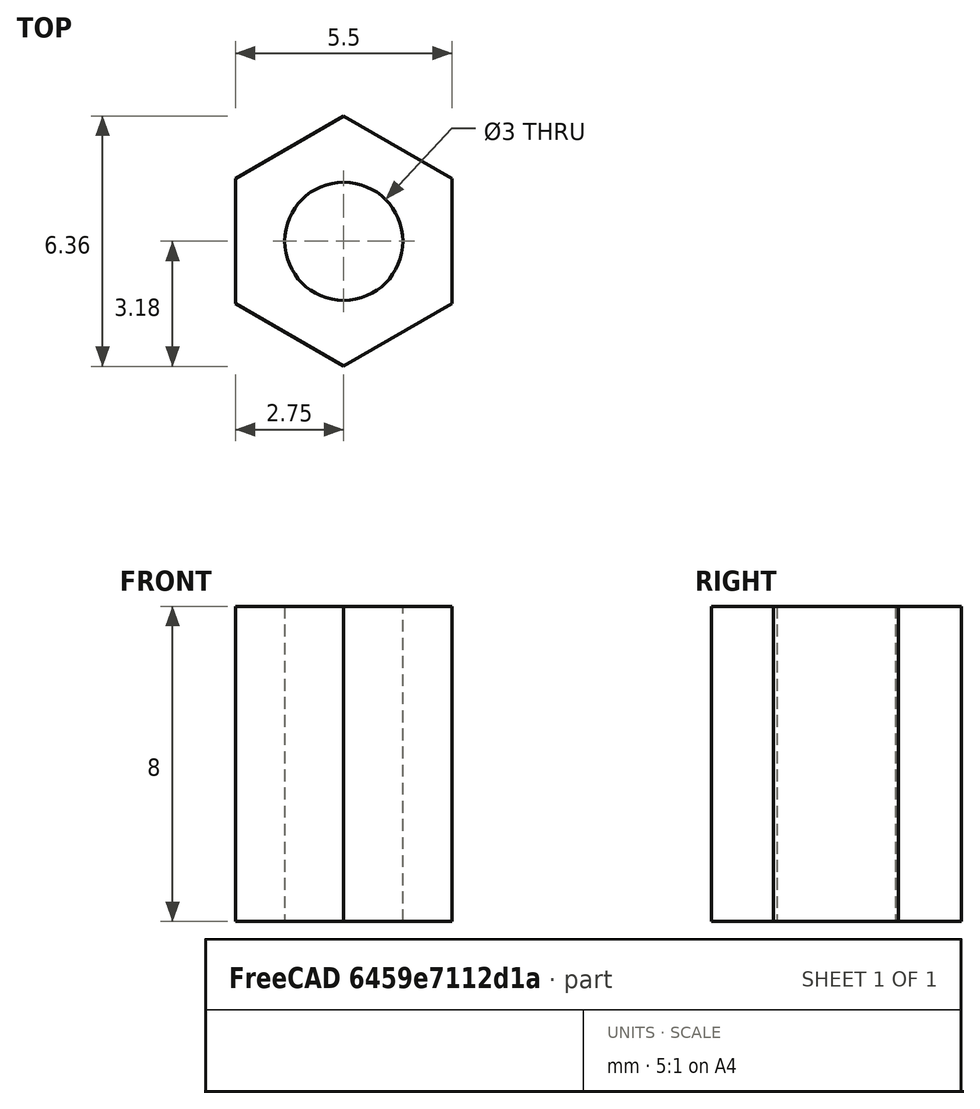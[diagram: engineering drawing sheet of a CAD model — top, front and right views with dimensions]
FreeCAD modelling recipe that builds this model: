
FCSTD DOCUMENT  (FreeCAD 0.20R29177 (Git))
Label: colonetteM3x8
License: All rights reserved
LicenseURL: http://en.wikipedia.org/wiki/All_rights_reserved
objects: Spreadsheet::Sheet×1, Sketcher::SketchObject×1, PartDesign::Pad×1, PartDesign::Body×1, App::Part×1
note: 4 computed .brp shape members not serialized (recipe doc carries the construction recipe); baked Part::Feature solids carry a one-line shape summary decoded from their .brp

FEATURE [Spreadsheet::Sheet] Spreadsheet  label="entretoiseM3x8Sp"
  cells = A2=long; B2(long)=8; A3=diam; B3(diam)=3; A4=hexaLarg; B4(hexaLarg)=5.5
FEATURE [Sketcher::SketchObject] Sketch
  FullyConstrained = true
  MapMode = 5
  Support = -> [XY_Plane001]
  expr: Constraints[20] = <<entretoiseM3x8Sp>>.diam
  expr: Constraints[21] = <<entretoiseM3x8Sp>>.hexaLarg
  sketch-geometry (8):
    g0: LineSegment StartX=0 StartY=3.17543 StartZ=0 EndX=-2.75 EndY=1.58771 EndZ=0
    g1: LineSegment StartX=-2.75 StartY=1.58771 StartZ=0 EndX=-2.75 EndY=-1.58771 EndZ=0
    g2: LineSegment StartX=-2.75 StartY=-1.58771 StartZ=0 EndX=-1.74905e-11 EndY=-3.17543 EndZ=0
    g3: LineSegment StartX=-1.74905e-11 StartY=-3.17543 StartZ=0 EndX=2.75 EndY=-1.58771 EndZ=0
    g4: LineSegment StartX=2.75 StartY=-1.58771 StartZ=0 EndX=2.75 EndY=1.58771 EndZ=0
    g5: LineSegment StartX=2.75 StartY=1.58771 StartZ=0 EndX=0 EndY=3.17543 EndZ=0
    g6: Circle CenterX=0 CenterY=0 CenterZ=0 NormalX=0 NormalY=0 NormalZ=1 AngleXU=0 Radius=3.17543
    g7: Circle CenterX=0 CenterY=0 CenterZ=0 NormalX=0 NormalY=0 NormalZ=1 AngleXU=0 Radius=1.5
  constraints (18):
    c: Coincident(g0,g1)
    c: Coincident(g1,g2)
    c: Coincident(g2,g3)
    c: Coincident(g3,g4)
    c: Coincident(g4,g5)
    c: Coincident(g5,g0)
    c: Equal(g0, g1-g5) x5
    c: PointOnObject(g0,g6)
    c: PointOnObject(g1,g6)
    c: PointOnObject(g2,g6)
    c: PointOnObject(g3,g6)
    c: PointOnObject(g4,g6)
    c: PointOnObject(g5,g6)
    c: Coincident(g6,g-1)
    c: PointOnObject(g5,g-2)
    c: Coincident(g7,g6)
    c: Diameter(g7) = 3
    c: DistanceX(g1,g3) = 5.5
FEATURE [PartDesign::Pad] Pad
  Direction = (0,0,1)
  Length = 8
  Length2 = 10
  Profile = -> Sketch
  ReferenceAxis = -> Sketch [N_Axis]
  Type = 0
  expr: Length = <<entretoiseM3x8Sp>>.long
FEATURE [PartDesign::Body] Body  label="entretoiseM3x8"
  Group = -> [Sketch,Pad]
  Origin = -> Origin001
  Tip = -> Pad
FEATURE [App::Part] Part  label="entretoiseM3x8Prt"
  Group = -> [Body]
  Origin = -> Origin
